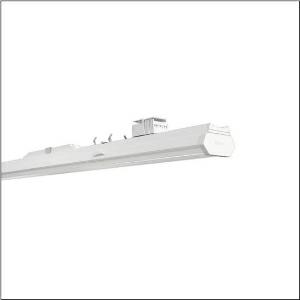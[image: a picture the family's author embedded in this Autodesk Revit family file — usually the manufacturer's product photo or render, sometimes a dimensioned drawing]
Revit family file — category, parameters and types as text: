
# Revit family: licross_21_protected_mo_52tp11dn4axg
name_source: partatom
category: Lighting Fixtures
units: mm (PartAtom-declared; Revit-internal decimal feet)

## family parameters
Cut with Voids When Loaded = No
Host = Face
Light Source = No
Part Type = Normal
Room Calculation Point = No
Round Connector Dimension = Use Diameter
Shared = No

## types (1)
- --- (1 x LED, 10000 lm, 57.8 W, 4000K)
    Apparent Load = 58 VA
    CIE Flux Codes = 83 94 98 100 100
    Color Rendering = 80
    Color Temperature = 4000K
    Default Elevation = 1800 mm
    Description = Licross 21 Protected MO, luminaire insert, of sheet steel, galvanised, coil coated, white, length: 1.500mm, width: 90mm, height: 103mm, LED rated luminous flux: 10.000lm, light colour: 840, SDCM (Standard Deviation of Colour Matching)MacAdam ≤ 3 SDCM (initial), control gear: DALI 2, with plug, 5-pole, with phase selection, mains connection: 220..240V, AC, 50/60Hz, rated input power: 58W, internal wiring halogen-free, primary light control with lens, of plastic, primary optical cover: cover, of PMMA, light emission: direct distribution, primary light characteristic: symmetric, protection rating (complete): IP64, insulation class (complete): insulation class I (protective earthing), certification: CE, ENEC, VDE, UKCA, protection symbol: D if used in an environment with conductive dust loads with corresponding accessories, impact resistance: IK06, permissible ambient temperature for indoor applications: -25..+40°C, corresponds to IFS (International Featured Standards) requirements for safety and quality in the food industry, reducing of maximum allowable ambient temperature of 5°C with ceiling mounting, LABS conformity tested according to VDMA 24364:2018-05, The light source and the operating device comply with the requirements of the Ecodesign Regulation (EU) 2019/2020 and are replaceable in accordance with this regulation, packaging unit: 1 piece
    Height = 92 mm
    Lamp = 1 x LED
    Lamp Light Flux = 10000 lm
    Lamp Power = 57.8 W
    Lamp count = 1
    Length = 1500 mm
    Luminous efficacy = 173 lm/W
    Manufacturer = Siteco
    ModVariant = No
    Model = 52TP11DN4AXG
    Mounting Place = Ceiling
    Mounting Type = Pendant
    Number of Poles = 1
    OnlyDefault = Yes
    Power Factor = 1
    Product Name = Licross 21 Protected MO
    Product group = luminaire insert | ceiling pendant
    ProductGroupID = 901
    Protection Class = Protection class I
    Protection Degree = IP 64
    RLX_Detail_Level = 1
    RLX_Emergency_Light_Flux = 0 lm
    RLX_Emergency_Type = 0
    RLX_Emergency_Type_DB = No
    RlxData = <blob elided: 24245 chars, md5=e8f013d0>
    Socket = socket
    Standby Power = 0 W
    System Light Flux = 10000 lm
    System Power = 58 W
    Type Comments = factory setting: luminous flux: 100 % | dim-lin: 254 | 390 mA
    Type Image = l_1256148.jpg
    URL = http://relux.com
    VarID = @adj_128299
    Voltage = 0 V
    Weight = 0.00 kg
    Width = 88 mm

## geometry (parser evidence)
native form markers: Blend x4, Sweep x11
no freeform markers — native parametric forms only
